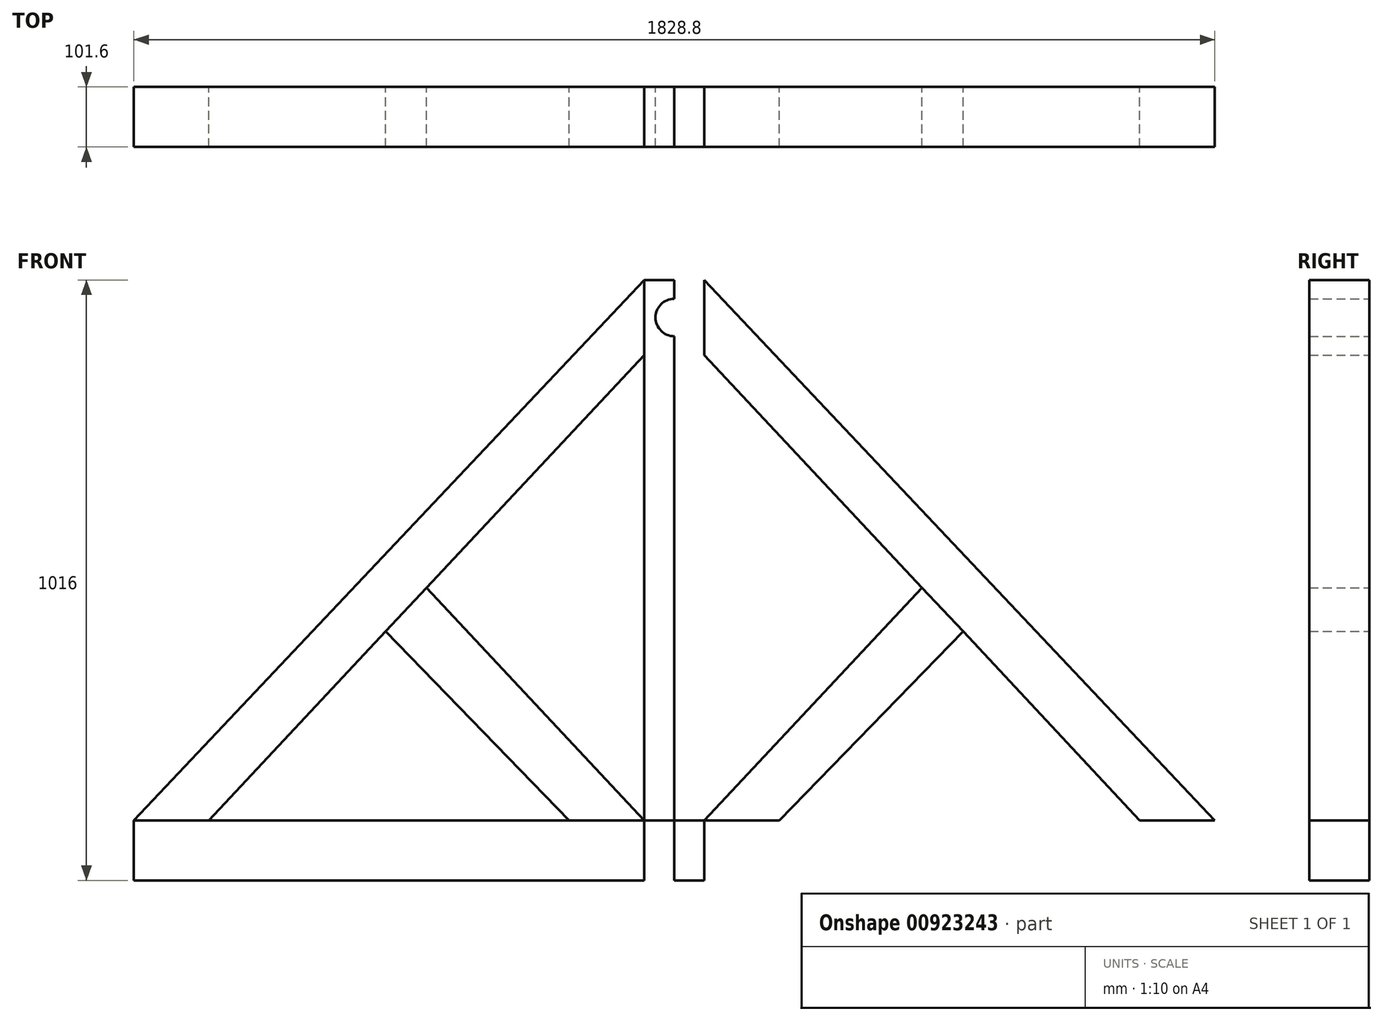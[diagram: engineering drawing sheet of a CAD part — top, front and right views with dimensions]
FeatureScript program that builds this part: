
annotation { "Feature Type Name" : "Feature", "Feature Type Description" : "" }
export const myFeature = defineFeature(function(context is Context, id is Id, definition is map)
    precondition{}
    {
        {
            var Q0;
            Q0=qCreatedBy(makeId("Front.planeOp"),FACE);
            var sketch = newSketch(context, id + "F0", { "sketchPlane" : qUnion([Q0])});
            skLineSegment(sketch, "E0", {"start": v(0, 594.9) * mm, "end": v(0, -421.1) * mm});
            skLineSegment(sketch, "E1.bottom", {"start": v(0, -421.1) * mm, "end": v(914.4, -421.1) * mm});
            skLineSegment(sketch, "E1.top", {"start": v(0, -319.5) * mm, "end": v(914.4, -319.5) * mm});
            skLineSegment(sketch, "E1.left", {"start": v(0, -421.1) * mm, "end": v(0, -319.5) * mm});
            skLineSegment(sketch, "E1.right", {"start": v(914.4, -421.1) * mm, "end": v(914.4, -319.5) * mm});
            skLineSegment(sketch, "E2.bottom", {"start": v(0, 594.9) * mm, "end": v(50.8, 594.9) * mm});
            skLineSegment(sketch, "E2.top", {"start": v(0, -421.1) * mm, "end": v(50.8, -421.1) * mm});
            skLineSegment(sketch, "E2.right", {"start": v(50.8, 594.9) * mm, "end": v(50.8, -421.1) * mm});
            skLineSegment(sketch, "E3", {"start": v(50.8, 594.9) * mm, "end": v(914.4, -319.5) * mm});
            skLineSegment(sketch, "E4", {"start": v(50.8, 467.9) * mm, "end": v(787.4, -319.5) * mm});
            skLineSegment(sketch, "E5", {"start": v(419.1, 74.2) * mm, "end": v(50.8, -319.5) * mm});
            skLineSegment(sketch, "E6", {"start": v(488.5, 0) * mm, "end": v(177.8, -319.5) * mm});
            skLineSegment(sketch, "E7.MirrorCS", {"start": v(0, 594.9) * mm, "end": v(-50.8, 594.9) * mm});
            skLineSegment(sketch, "E8.MirrorCS", {"start": v(0, -421.1) * mm, "end": v(-50.8, -421.1) * mm});
            skLineSegment(sketch, "E9.MirrorCS", {"start": v(-50.8, 467.9) * mm, "end": v(-787.4, -319.5) * mm});
            skLineSegment(sketch, "E10.MirrorCS", {"start": v(-419.1, 74.2) * mm, "end": v(-50.8, -319.5) * mm});
            skLineSegment(sketch, "E11.MirrorCS", {"start": v(0, -421.1) * mm, "end": v(-914.4, -421.1) * mm});
            skLineSegment(sketch, "E12.MirrorCS", {"start": v(-50.8, 594.9) * mm, "end": v(-50.8, -421.1) * mm});
            skLineSegment(sketch, "E13.MirrorCS", {"start": v(0, -319.5) * mm, "end": v(-914.4, -319.5) * mm});
            skLineSegment(sketch, "E14.MirrorCS", {"start": v(-914.4, -421.1) * mm, "end": v(-914.4, -319.5) * mm});
            skLineSegment(sketch, "E15.MirrorCS", {"start": v(-488.5, 0) * mm, "end": v(-177.8, -319.5) * mm});
            skLineSegment(sketch, "E16.MirrorCS", {"start": v(-50.8, 594.9) * mm, "end": v(-914.4, -319.5) * mm});
            skCircle(sketch, "E17", {"center": v(0, 531.4) * mm, "radius": 31.75 * mm});
            skSolve(sketch);
        }
        {
            var Q0;
            {var subQ4=sQuery(id+"F0.wireOp",EDGE,"E16.MirrorCS");Q0=makeQuery(id+"F0.imprint","IMPRINT",FACE,{"disambiguationData":[TD([[makeQuery(id+"F0.imprint","IMPRINT",EDGE,{"derivedFrom":subQ4}),1.0]])]});}
            var Q1;
            {var subQ0=sQuery(id+"F0.wireOp",EDGE,"E10.MirrorCS");Q1=makeQuery(id+"F0.imprint","IMPRINT",FACE,{"disambiguationData":[TD([[makeQuery(id+"F0.imprint","IMPRINT",EDGE,{"derivedFrom":subQ0}),-1.0]])]});}
            var Q2;
            {var subQ7=sQuery(id+"F0.wireOp",EDGE,"E14.MirrorCS");Q2=makeQuery(id+"F0.imprint","IMPRINT",FACE,{"disambiguationData":[TD([[makeQuery(id+"F0.imprint","IMPRINT",EDGE,{"derivedFrom":subQ7}),-1.0]])]});}
            var Q3;
            {var subQ5=sQuery(id+"F0.wireOp",EDGE,"E7.MirrorCS");Q3=makeQuery(id+"F0.imprint","IMPRINT",FACE,{"disambiguationData":[TD([[makeQuery(id+"F0.imprint","IMPRINT",EDGE,{"derivedFrom":subQ5}),1.0]])]});}
            var Q4;
            {var subQ8=sQuery(id+"F0.wireOp",EDGE,"E2.bottom");Q4=makeQuery(id+"F0.imprint","IMPRINT",FACE,{"disambiguationData":[TD([[makeQuery(id+"F0.imprint","IMPRINT",EDGE,{"derivedFrom":subQ8}),-1.0]])]});}
            var Q5;
            {var subQ4=sQuery(id+"F0.wireOp",EDGE,"E2.top");Q5=makeQuery(id+"F0.imprint","IMPRINT",FACE,{"disambiguationData":[TD([[makeQuery(id+"F0.imprint","IMPRINT",EDGE,{"derivedFrom":subQ4}),1.0]])]});}
            var Q6;
            {var subQ0=sQuery(id+"F0.wireOp",EDGE,"E1.left");Q6=makeQuery(id+"F0.imprint","IMPRINT",FACE,{"disambiguationData":[TD([[makeQuery(id+"F0.imprint","IMPRINT",EDGE,{"derivedFrom":subQ0}),1.0]])]});}
            var Q7;
            {var subQ6=sQuery(id+"F0.wireOp",EDGE,"E1.bottom");Q7=makeQuery(id+"F0.imprint","IMPRINT",FACE,{"disambiguationData":[TD([[makeQuery(id+"F0.imprint","IMPRINT",EDGE,{"derivedFrom":subQ6}),1.0]])]});}
            var Q8;
            {var subQ4=sQuery(id+"F0.wireOp",EDGE,"E3");Q8=makeQuery(id+"F0.imprint","IMPRINT",FACE,{"disambiguationData":[TD([[makeQuery(id+"F0.imprint","IMPRINT",EDGE,{"derivedFrom":subQ4}),-1.0]])]});}
            var Q9;
            {var subQ0=sQuery(id+"F0.wireOp",EDGE,"E5");Q9=makeQuery(id+"F0.imprint","IMPRINT",FACE,{"disambiguationData":[TD([[makeQuery(id+"F0.imprint","IMPRINT",EDGE,{"derivedFrom":subQ0}),1.0]])]});}
            extrude(context, id + "F1", {"entities" : qUnion([Q0, Q1, Q2, Q3, Q4, Q5, Q6, Q7, Q8, Q9]), "depth" : 101.6 * mm, "offsetDistance" : 25.4 * mm, "symmetric" : true});
        }
    });
